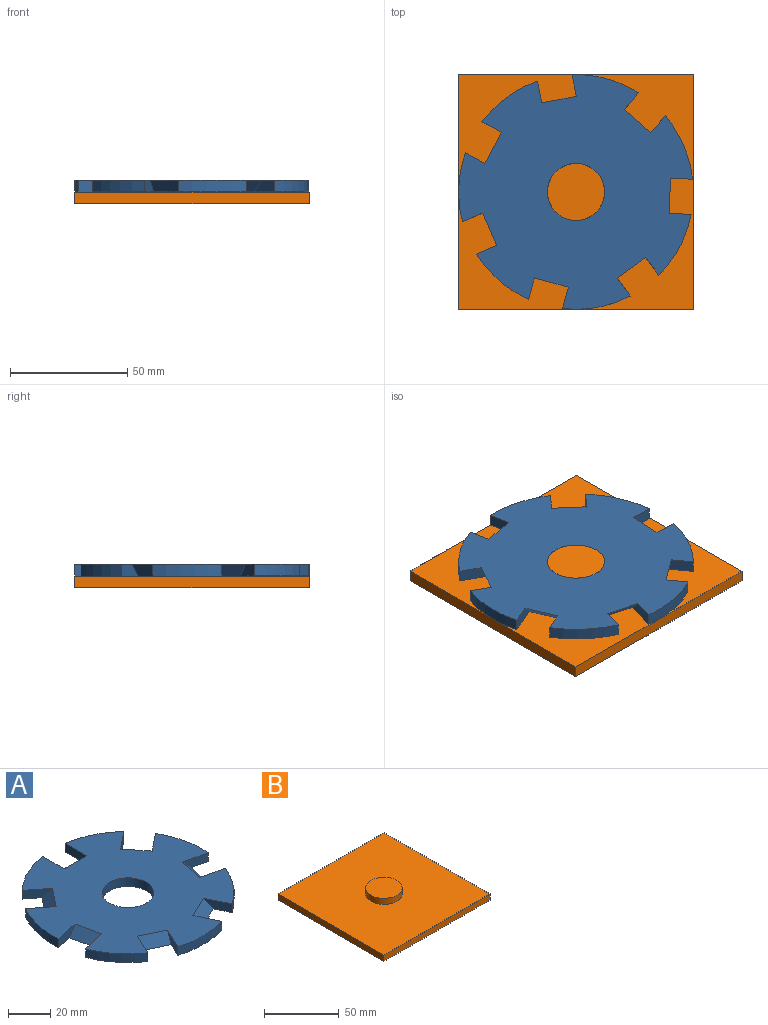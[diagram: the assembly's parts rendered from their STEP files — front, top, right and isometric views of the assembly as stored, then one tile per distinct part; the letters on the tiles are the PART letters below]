
ASSEMBLY  parts=2 mates=1
PART A: 31 faces, bbox 100x99.4x5 mm
  f0: cylinder r=50mm len=28.65mm, axis (0,0,-1), area 149.1mm2, adj f1,f5,f19,f20
  f1: plane 11.29x9mm, normal (0.62,0.78,0), area 59.7mm2, adj f0,f19,f20,f28
  f2: plane 11.29x9mm, normal (-0.62,-0.78,0), area 59.7mm2, adj f18,f19,f20,f28
  f3: cylinder r=50mm len=22.97mm, axis (0,0,-1), area 149.1mm2, adj f4,f8,f19,f20
  f4: plane 14.07x5mm, normal (-0.22,0.97,0), area 59.7mm2, adj f3,f19,f20,f29
  f5: plane 14.07x5mm, normal (0.22,-0.97,0), area 59.7mm2, adj f0,f19,f20,f29
  f6: cylinder r=50mm len=29.38mm, axis (0,0,-1), area 149.1mm2, adj f7,f11,f19,f20
  f7: plane 13.01x6.26mm, normal (-0.9,0.43,0), area 59.7mm2, adj f6,f19,f20,f30
  f8: plane 13.01x6.26mm, normal (0.9,-0.43,0), area 59.7mm2, adj f3,f19,f20,f30
  f9: cylinder r=50mm len=22.97mm, axis (0,0,-1), area 149.1mm2, adj f10,f14,f19,f20
  f10: plane 13.01x6.26mm, normal (-0.9,-0.43,0), area 59.7mm2, adj f9,f19,f20,f24
  f11: plane 13.01x6.26mm, normal (0.9,0.43,0), area 59.7mm2, adj f6,f19,f20,f24
  f12: cylinder r=50mm len=28.65mm, axis (0,0,-1), area 149.1mm2, adj f13,f17,f19,f20
  f13: plane 14.07x5mm, normal (-0.22,-0.97,0), area 59.7mm2, adj f12,f19,f20,f25
  f14: plane 14.07x5mm, normal (0.22,0.97,0), area 59.7mm2, adj f9,f19,f20,f25
  f15: cylinder r=50mm len=26.47mm, axis (0,0,-1), area 149.1mm2, adj f16,f19,f20,f23
  f16: plane 11.29x9mm, normal (0.62,-0.78,0), area 59.7mm2, adj f15,f19,f20,f26
  f17: plane 11.29x9mm, normal (-0.62,0.78,0), area 59.7mm2, adj f12,f19,f20,f26
  f18: cylinder r=50mm len=26.47mm, axis (0,0,-1), area 149.1mm2, adj f2,f19,f20,f22
  f19: plane 100x99.43mm, normal (0,0,1), area 5834.8mm2, adj f0,f1,f2,f3,f4,f5,f6,f7
  f20: plane 100x99.43mm, normal (0,0,-1), area 6359.8mm2, adj f0,f1,f2,f3,f4,f5,f6,f7
  f21: cylinder r=12.15mm len=24.31mm, axis (0,0,-1), area 381.8mm2, adj f19,f20
  f22: plane 14.43x5mm, normal (1,0,0), area 59.7mm2, adj f18,f19,f20,f27
  f23: plane 14.43x5mm, normal (-1,0,0), area 59.7mm2, adj f15,f19,f20,f27
  f24: plane 15.68x11.01mm, normal (0.31,-0.64,0.71), area 106.1mm2, adj f10,f11,f19,f20
  f25: plane 15.74x8.21mm, normal (0.69,-0.16,0.71), area 106.1mm2, adj f13,f14,f19,f20
  f26: plane 14.85x13.26mm, normal (0.55,0.44,0.71), area 106.1mm2, adj f16,f17,f19,f20
  f27: plane 15x5mm, normal (0,0.71,0.71), area 106.1mm2, adj f19,f20,f22,f23
  f28: plane 14.85x13.26mm, normal (-0.55,0.44,0.71), area 106.1mm2, adj f1,f2,f19,f20
  f29: plane 15.74x8.21mm, normal (-0.69,-0.16,0.71), area 106.1mm2, adj f4,f5,f19,f20
  f30: plane 15.68x11.01mm, normal (-0.31,-0.64,0.71), area 106.1mm2, adj f7,f8,f19,f20
PART B: 8 faces, bbox 100x100x10 mm
  f0: plane 100x5mm, normal (0,-1,0), area 500mm2, adj f1,f3,f4,f5
  f1: plane 100x5mm, normal (1,0,0), area 500mm2, adj f0,f2,f4,f5
  f2: plane 100x5mm, normal (0,1,0), area 500mm2, adj f1,f3,f4,f5
  f3: plane 100x5mm, normal (-1,0,0), area 500mm2, adj f0,f2,f4,f5
  f4: plane 100x100mm, normal (0,0,-1), area 10000mm2, adj f0,f1,f2,f3
  f5: plane 100x100mm, normal (0,0,1), area 9536mm2, adj f0,f1,f2,f3,f6
  f6: cylinder r=12.15mm len=24.31mm, axis (0,0,-1), area 381.8mm2, adj f5,f7
  f7: plane 24.31x24.31mm, normal (0,0,1), area 464mm2, adj f6
PLACE A rot(axis=(0.84,-0.55,0),180deg) t=(0,0,5)mm
PLACE B at identity fixed
MATE revolute A.f0 <-> B.f6  axis (0,0,-1) through (0,0,0)mm
